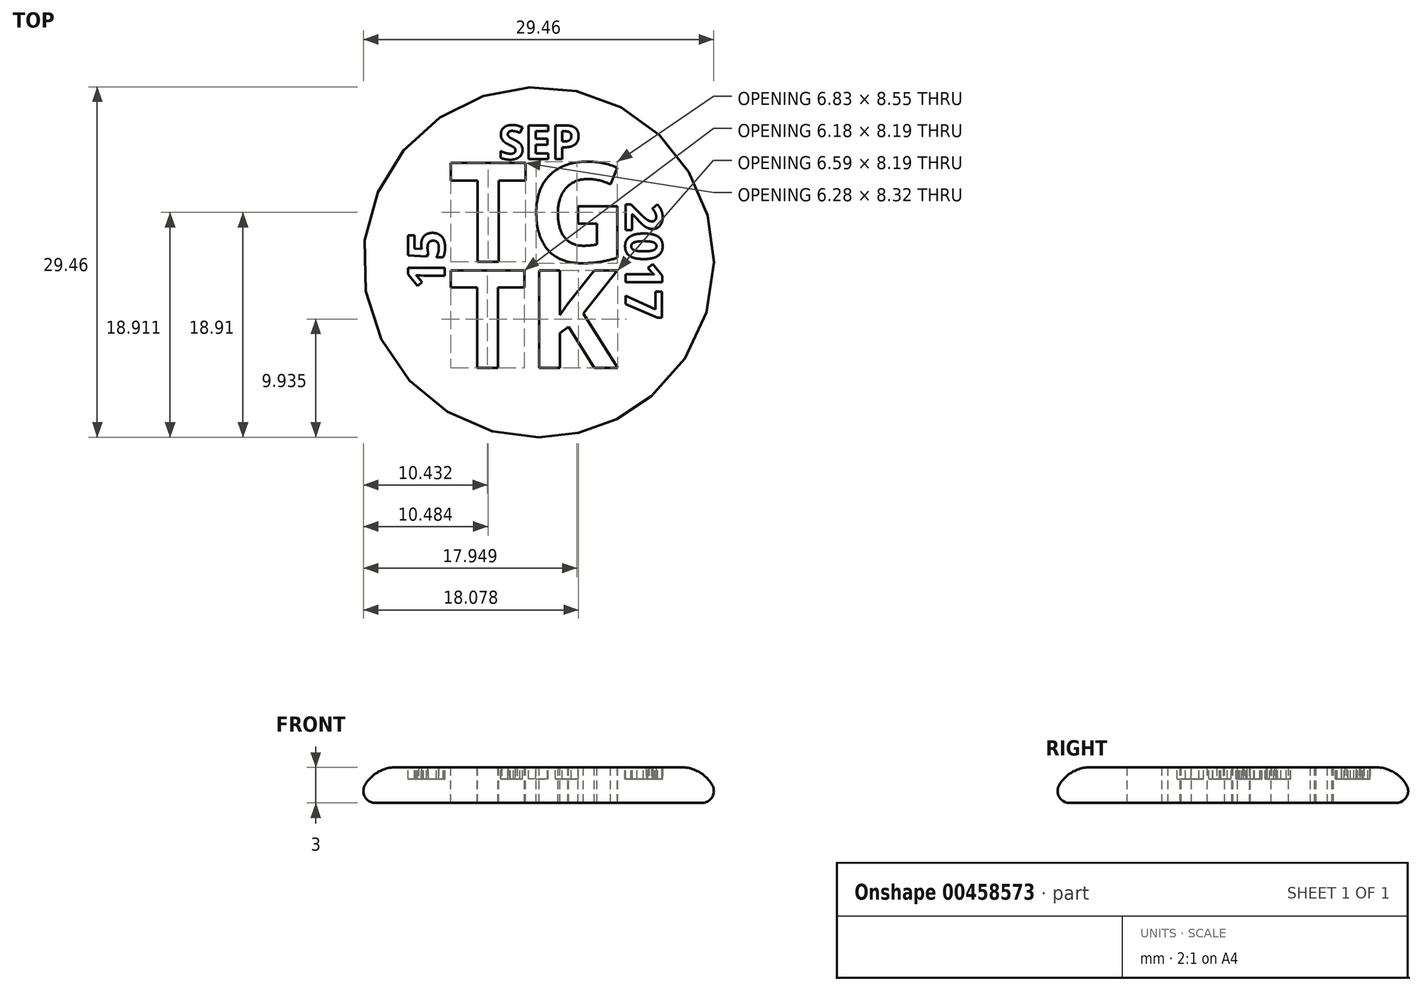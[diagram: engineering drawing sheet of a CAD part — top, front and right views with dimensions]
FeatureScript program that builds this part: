
annotation { "Feature Type Name" : "Feature", "Feature Type Description" : "" }
export const myFeature = defineFeature(function(context is Context, id is Id, definition is map)
    precondition{}
    {
        {
            var Q0;
            Q0=qCreatedBy(makeId("Top.planeOp"),FACE);
            var sketch = newSketch(context, id + "F0", { "sketchPlane" : qUnion([Q0])});
            skEllipse(sketch, "E0", {"center": v(0, 0) * mm, "majorRadius": 15 * mm, "minorRadius": 15 * mm, "majorAxis": v(1, 0)});
            skSolve(sketch);
        }
        {
            var Q0;
            Q0 = qSketchRegion(id + "F0", true);
            extrude(context, id + "F1", {"entities" : qUnion([Q0]), "depth" : 3 * mm, "offsetDistance" : 25 * mm});
        }
        {
            var Q0;
            Q0=makeQuery(id+"F1.opExtrude","CAP_FACE",FACE,{"disambiguationData":[OSD([sQuery(id+"F0.wireOp",EDGE,"E0")])],"isStart":false});
            fillet(context, id + "F2", {"entities" : qUnion([Q0]), "radius" : 3 * mm, "tangentPropagation" : true, "allowEdgeOverflow" : false});
        }
        {
            var Q0;
            Q0=makeQuery(id+"F1.opExtrude","CAP_FACE",FACE,{"disambiguationData":[OSD([sQuery(id+"F0.wireOp",EDGE,"E0")])],"isStart":false});
            var sketch = newSketch(context, id + "F3", { "sketchPlane" : qUnion([Q0])});
            skText(sketch, "E1", { "text": "TG", "fontName": "OpenSans-Bold.ttf"});
            skText(sketch, "E2", { "text": "TK", "fontName": "OpenSans-Bold.ttf"});
            const initialGuessF3  = {"E1": [-0.00762, 2e-05, 1, 0, 0.00839], "E2": [-0.00762, -0.00889, 1, 0, 0.00826]};
            skSetInitialGuess(sketch, initialGuessF3);
            skSolve(sketch);
        }
        {
            var Q0;
            Q0 = qSketchRegion(id + "F3", true);
            extrude(context, id + "F4", {"entities" : qUnion([Q0]), "operationType" : NewBodyOperationType.REMOVE, "oppositeDirection" : true, "depth" : 3 * mm, "offsetDistance" : 25 * mm});
        }
        {
            var Q0;
            Q0=makeQuery(id+"F1.opExtrude","CAP_FACE",FACE,{"disambiguationData":[OSD([sQuery(id+"F0.wireOp",EDGE,"E0")])],"isStart":false});
            var sketch = newSketch(context, id + "F5", { "sketchPlane" : qUnion([Q0])});
            skText(sketch, "E3", { "text": "15", "fontName": "OpenSans-Bold.ttf"});
            skText(sketch, "E4", { "text": "SEP", "fontName": "OpenSans-Bold.ttf"});
            skText(sketch, "E5", { "text": "2017", "fontName": "OpenSans-Bold.ttf"});
            const initialGuessF5  = {"E3": [-0.0079, -0.00226, 0, 1, 0.0031], "E4": [-0.00339, 0.00865, 1, 0, 0.00287], "E5": [0.00731, 0.00502, 0, -1, 0.0031]};
            skSetInitialGuess(sketch, initialGuessF5);
            skSolve(sketch);
        }
        {
            var Q0;
            Q0 = qSketchRegion(id + "F5", true);
            extrude(context, id + "F6", {"entities" : qUnion([Q0]), "operationType" : NewBodyOperationType.REMOVE, "oppositeDirection" : true, "depth" : 1 * mm, "offsetDistance" : 25 * mm});
        }
        {
            var Q0;
            {var subQ0=sQuery(id+"F0.wireOp",EDGE,"E0");Q0=makeQuery(id+"F2.opFillet","BLEND_EDGE",EDGE,{"blendedFrom":[makeQuery(id+"F1.opExtrude","CAP_EDGE",EDGE,{"disambiguationData":[OSD([subQ0])],"isStart":false}),makeQuery(id+"F1.opExtrude","CAP_FACE",FACE,{"disambiguationData":[OSD([subQ0])],"isStart":true})],"blendedInto":[makeQuery(id+"F1.opExtrude","CAP_FACE",FACE,{"disambiguationData":[OSD([subQ0])],"isStart":true})]});}
            fillet(context, id + "F7", {"entities" : qUnion([Q0]), "radius" : 1 * mm, "tangentPropagation" : true, "allowEdgeOverflow" : false});
        }
    });
